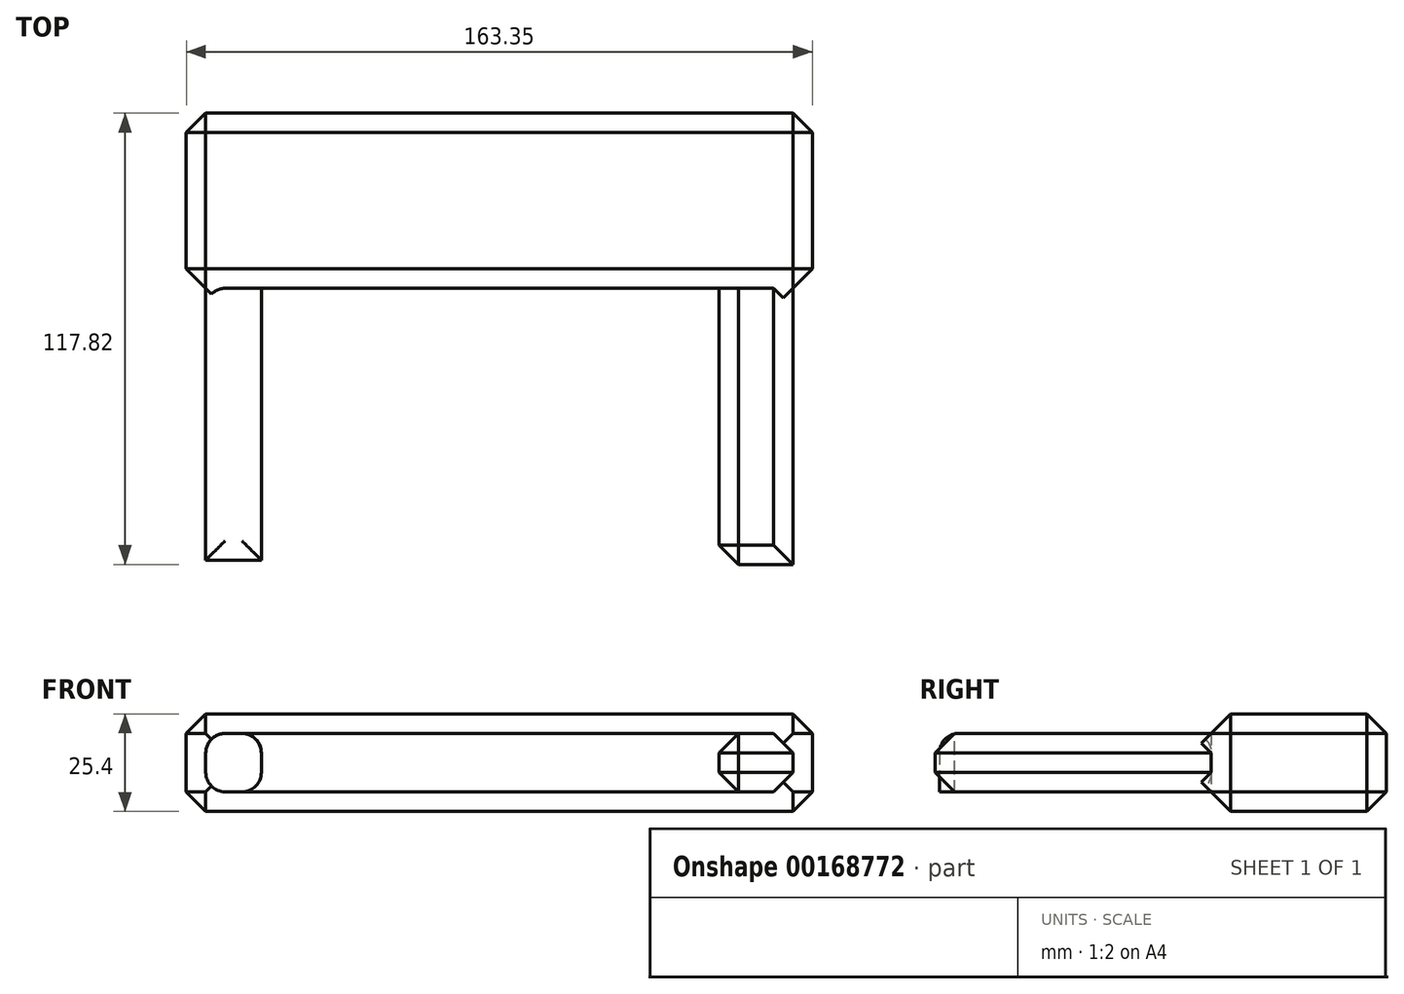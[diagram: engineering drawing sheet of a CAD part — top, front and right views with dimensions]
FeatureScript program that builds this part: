
annotation { "Feature Type Name" : "Feature", "Feature Type Description" : "" }
export const myFeature = defineFeature(function(context is Context, id is Id, definition is map)
    precondition{}
    {
        {
            var Q0;
            Q0=qCreatedBy(makeId("Top.planeOp"),FACE);
            var sketch = newSketch(context, id + "F0", { "sketchPlane" : qUnion([Q0])});
            skLineSegment(sketch, "E0.bottom", {"start": v(-41.95, 0) * mm, "end": v(121.4, 0) * mm});
            skLineSegment(sketch, "E0.top", {"start": v(-41.95, 45.73) * mm, "end": v(121.4, 45.73) * mm});
            skLineSegment(sketch, "E0.left", {"start": v(-41.95, 0) * mm, "end": v(-41.95, 45.73) * mm});
            skLineSegment(sketch, "E0.right", {"start": v(121.4, 0) * mm, "end": v(121.4, 45.73) * mm});
            skPoint(sketch, "E0.middle", {"position": v(39.72, 22.86) * mm});
            skSolve(sketch);
        }
        {
            var Q0;
            Q0 = qSketchRegion(id + "F0", true);
            extrude(context, id + "F1", {"entities" : qUnion([Q0]), "depth" : 25.4 * mm});
        }
        {
            var Q0;
            Q0=makeQuery(id+"F1.opExtrude","CAP_EDGE",EDGE,{"disambiguationData":[OSD([sQuery(id+"F0.wireOp",EDGE,"E0.right")])],"isStart":false});
            var Q1;
            Q1=makeQuery(id+"F1.opExtrude","CAP_EDGE",EDGE,{"disambiguationData":[OSD([sQuery(id+"F0.wireOp",EDGE,"E0.right")])],"isStart":true});
            var Q2;
            Q2=makeQuery(id+"F1.opExtrude","CAP_EDGE",EDGE,{"disambiguationData":[OSD([sQuery(id+"F0.wireOp",EDGE,"E0.bottom")])],"isStart":true});
            var Q3;
            Q3=makeQuery(id+"F1.opExtrude","SWEPT_EDGE",EDGE,{"disambiguationData":[OSD([sQuery(id+"F0.wireOp",EDGE,"E0.bottom"),sQuery(id+"F0.wireOp",EDGE,"E0.right")])]});
            var Q4;
            Q4=makeQuery(id+"F1.opExtrude","SWEPT_EDGE",EDGE,{"disambiguationData":[OSD([sQuery(id+"F0.wireOp",EDGE,"E0.top"),sQuery(id+"F0.wireOp",EDGE,"E0.right")])]});
            var Q5;
            Q5=makeQuery(id+"F1.opExtrude","CAP_EDGE",EDGE,{"disambiguationData":[OSD([sQuery(id+"F0.wireOp",EDGE,"E0.top")])],"isStart":true});
            var Q6;
            Q6=makeQuery(id+"F1.opExtrude","CAP_EDGE",EDGE,{"disambiguationData":[OSD([sQuery(id+"F0.wireOp",EDGE,"E0.top")])],"isStart":false});
            var Q7;
            Q7=makeQuery(id+"F1.opExtrude","CAP_EDGE",EDGE,{"disambiguationData":[OSD([sQuery(id+"F0.wireOp",EDGE,"E0.left")])],"isStart":false});
            var Q8;
            Q8=makeQuery(id+"F1.opExtrude","SWEPT_EDGE",EDGE,{"disambiguationData":[OSD([sQuery(id+"F0.wireOp",EDGE,"E0.bottom"),sQuery(id+"F0.wireOp",EDGE,"E0.left")])]});
            var Q9;
            Q9=makeQuery(id+"F1.opExtrude","CAP_EDGE",EDGE,{"disambiguationData":[OSD([sQuery(id+"F0.wireOp",EDGE,"E0.left")])],"isStart":true});
            var Q10;
            Q10=makeQuery(id+"F1.opExtrude","SWEPT_EDGE",EDGE,{"disambiguationData":[OSD([sQuery(id+"F0.wireOp",EDGE,"E0.top"),sQuery(id+"F0.wireOp",EDGE,"E0.left")])]});
            var Q11;
            Q11=makeQuery(id+"F1.opExtrude","CAP_FACE",FACE,{"disambiguationData":[OSD([sQuery(id+"F0.wireOp",EDGE,"E0.bottom"),sQuery(id+"F0.wireOp",EDGE,"E0.top"),sQuery(id+"F0.wireOp",EDGE,"E0.left"),sQuery(id+"F0.wireOp",EDGE,"E0.right")])],"isStart":false});
            chamfer(context, id + "F2", {"entities" : qUnion([Q0, Q1, Q2, Q3, Q4, Q5, Q6, Q7, Q8, Q9, Q10, Q11]), "width" : 5.08 * mm, "tangentPropagation" : true});
        }
        {
            var Q0;
            Q0=makeQuery(id+"F1.opExtrude","SWEPT_FACE",FACE,{"disambiguationData":[OSD([sQuery(id+"F0.wireOp",EDGE,"E0.bottom")])]});
            var sketch = newSketch(context, id + "F3", { "sketchPlane" : qUnion([Q0])});
            skLineSegment(sketch, "E1", {"start": v(-36.87, 5.08) * mm, "end": v(-36.87, 20.32) * mm});
            skLineSegment(sketch, "E2", {"start": v(-36.87, 20.32) * mm, "end": v(-22.37, 20.32) * mm});
            skLineSegment(sketch, "E3", {"start": v(-22.37, 20.32) * mm, "end": v(-22.37, 5.08) * mm});
            skLineSegment(sketch, "E4", {"start": v(-22.37, 5.08) * mm, "end": v(-36.87, 5.08) * mm});
            skSolve(sketch);
        }
        {
            var Q0;
            Q0 = qSketchRegion(id + "F3", true);
            extrude(context, id + "F4", {"entities" : qUnion([Q0]), "operationType" : NewBodyOperationType.ADD, "depth" : 70.94 * mm});
        }
        {
            var Q0;
            Q0=makeQuery(id+"F1.opExtrude","SWEPT_FACE",FACE,{"disambiguationData":[OSD([sQuery(id+"F0.wireOp",EDGE,"E0.bottom")])]});
            var sketch = newSketch(context, id + "F5", { "sketchPlane" : qUnion([Q0])});
            skLineSegment(sketch, "E5", {"start": v(116.32, 20.32) * mm, "end": v(96.99, 20.32) * mm});
            skLineSegment(sketch, "E6", {"start": v(96.99, 20.32) * mm, "end": v(96.99, 5.08) * mm});
            skLineSegment(sketch, "E7", {"start": v(96.99, 5.08) * mm, "end": v(116.32, 5.08) * mm});
            skLineSegment(sketch, "E8", {"start": v(116.32, 5.08) * mm, "end": v(116.32, 20.32) * mm});
            skSolve(sketch);
        }
        {
            var Q0;
            Q0 = qSketchRegion(id + "F5", true);
            extrude(context, id + "F6", {"entities" : qUnion([Q0]), "operationType" : NewBodyOperationType.ADD, "depth" : 72.1 * mm});
        }
        {
            var Q0;
            Q0=makeQuery(id+"F4.opExtrude","SWEPT_EDGE",EDGE,{"disambiguationData":[OSD([sQuery(id+"F3.wireOp",EDGE,"E1"),sQuery(id+"F3.wireOp",EDGE,"E2")])]});
            var Q1;
            Q1=makeQuery(id+"F4.opExtrude","SWEPT_EDGE",EDGE,{"disambiguationData":[OSD([sQuery(id+"F0.wireOp",EDGE,"E0.bottom"),sQuery(id+"F3.wireOp",EDGE,"E3"),sQuery(id+"F3.wireOp",EDGE,"E4")])]});
            var Q2;
            Q2=makeQuery(id+"F4.opExtrude","SWEPT_EDGE",EDGE,{"disambiguationData":[OSD([sQuery(id+"F0.wireOp",EDGE,"E0.bottom"),sQuery(id+"F3.wireOp",EDGE,"E2"),sQuery(id+"F3.wireOp",EDGE,"E3")])]});
            var Q3;
            Q3=makeQuery(id+"F4.opExtrude","CAP_EDGE",EDGE,{"disambiguationData":[OSD([sQuery(id+"F3.wireOp",EDGE,"E2")])],"isStart":false});
            var Q4;
            Q4=makeQuery(id+"F4.opExtrude","SWEPT_EDGE",EDGE,{"disambiguationData":[OSD([sQuery(id+"F3.wireOp",EDGE,"E1"),sQuery(id+"F3.wireOp",EDGE,"E4")])]});
            fillet(context, id + "F7", {"entities" : qUnion([Q0, Q1, Q2, Q3, Q4]), "radius" : 5.08 * mm, "tangentPropagation" : true, "allowEdgeOverflow" : false});
        }
        {
            var Q0;
            Q0=makeQuery(id+"F6.opExtrude","SWEPT_EDGE",EDGE,{"disambiguationData":[OSD([sQuery(id+"F0.wireOp",EDGE,"E0.bottom"),sQuery(id+"F5.wireOp",EDGE,"E5"),sQuery(id+"F5.wireOp",EDGE,"E6")])]});
            var Q1;
            Q1=makeQuery(id+"F6.opExtrude","SWEPT_EDGE",EDGE,{"disambiguationData":[OSD([sQuery(id+"F5.wireOp",EDGE,"E5"),sQuery(id+"F5.wireOp",EDGE,"E8")])]});
            var Q2;
            Q2=makeQuery(id+"F6.opExtrude","SWEPT_EDGE",EDGE,{"disambiguationData":[OSD([sQuery(id+"F0.wireOp",EDGE,"E0.bottom"),sQuery(id+"F5.wireOp",EDGE,"E6"),sQuery(id+"F5.wireOp",EDGE,"E7")])]});
            var Q3;
            Q3=makeQuery(id+"F6.opExtrude","CAP_EDGE",EDGE,{"disambiguationData":[OSD([sQuery(id+"F5.wireOp",EDGE,"E5")])],"isStart":false});
            var Q4;
            Q4=makeQuery(id+"F6.opExtrude","CAP_EDGE",EDGE,{"disambiguationData":[OSD([sQuery(id+"F5.wireOp",EDGE,"E7")])],"isStart":false});
            var Q5;
            Q5=makeQuery(id+"F6.opExtrude","CAP_EDGE",EDGE,{"disambiguationData":[OSD([sQuery(id+"F5.wireOp",EDGE,"E6")])],"isStart":false});
            var Q6;
            Q6=makeQuery(id+"F6.opExtrude","SWEPT_EDGE",EDGE,{"disambiguationData":[OSD([sQuery(id+"F5.wireOp",EDGE,"E7"),sQuery(id+"F5.wireOp",EDGE,"E8")])]});
            chamfer(context, id + "F8", {"entities" : qUnion([Q0, Q1, Q2, Q3, Q4, Q5, Q6]), "width" : 5.08 * mm, "tangentPropagation" : true});
        }
    });
